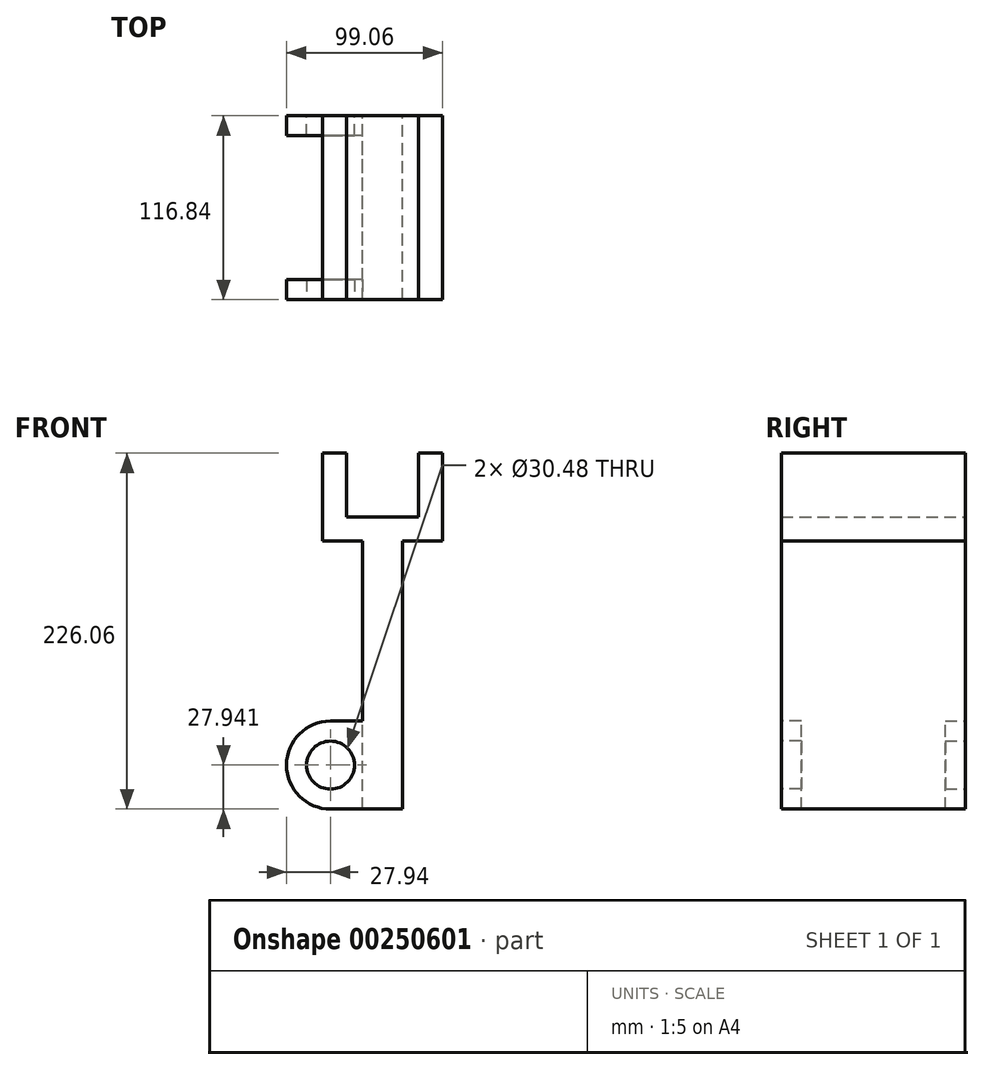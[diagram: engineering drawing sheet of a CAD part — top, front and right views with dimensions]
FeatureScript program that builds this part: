
annotation { "Feature Type Name" : "Feature", "Feature Type Description" : "" }
export const myFeature = defineFeature(function(context is Context, id is Id, definition is map)
    precondition{}
    {
        {
            var Q0;
            Q0=qCreatedBy(makeId("Front.planeOp"),FACE);
            var sketch = newSketch(context, id + "F0", { "sketchPlane" : qUnion([Q0])});
            skLineSegment(sketch, "E0", {"start": v(0, 86.1) * mm, "end": v(-38.1, 86.1) * mm});
            skLineSegment(sketch, "E1", {"start": v(-38.1, 86.1) * mm, "end": v(-38.1, 141.98) * mm});
            skLineSegment(sketch, "E2", {"start": v(-38.1, 141.98) * mm, "end": v(-22.86, 141.98) * mm});
            skLineSegment(sketch, "E3", {"start": v(-22.86, 141.98) * mm, "end": v(-22.86, 101.34) * mm});
            skLineSegment(sketch, "E4", {"start": v(-22.86, 101.34) * mm, "end": v(0, 101.34) * mm});
            skLineSegment(sketch, "E5", {"start": v(0, 163.08) * mm, "end": v(0, 27.94) * mm, "construction": true});
            skLineSegment(sketch, "E6.MirrorCS", {"start": v(0, 86.1) * mm, "end": v(38.1, 86.1) * mm});
            skLineSegment(sketch, "E7.MirrorCS", {"start": v(38.1, 86.1) * mm, "end": v(38.1, 141.98) * mm});
            skLineSegment(sketch, "E8.MirrorCS", {"start": v(38.1, 141.98) * mm, "end": v(22.86, 141.98) * mm});
            skLineSegment(sketch, "E9.MirrorCS", {"start": v(22.86, 141.98) * mm, "end": v(22.86, 101.34) * mm});
            skLineSegment(sketch, "E10.MirrorCS", {"start": v(22.86, 101.34) * mm, "end": v(0, 101.34) * mm});
            skSolve(sketch);
        }
        {
            var Q0;
            Q0=makeQuery(id+"F0.imprint","IMPRINT",FACE,{"disambiguationData":[TD([[makeQuery(id+"F0.imprint","IMPRINT",EDGE,{"derivedFrom":sQuery(id+"F0.wireOp",EDGE,"E0")}),-1.0]])]});
            extrude(context, id + "F1", {"entities" : qUnion([Q0]), "depth" : 116.84 * mm});
        }
        {
            var Q0;
            Q0=makeQuery(id+"F1.opExtrude","SWEPT_FACE",FACE,{"disambiguationData":[OSD([sQuery(id+"F0.wireOp",EDGE,"E0"),sQuery(id+"F0.wireOp",EDGE,"E6.MirrorCS")])]});
            var sketch = newSketch(context, id + "F2", { "sketchPlane" : qUnion([Q0])});
            skPoint(sketch, "E11.middle", {"position": v(0, 82.12) * mm});
            skLineSegment(sketch, "E12.bottom", {"start": v(12.7, 116.84) * mm, "end": v(-12.7, 116.84) * mm});
            skLineSegment(sketch, "E12.top", {"start": v(12.7, 0) * mm, "end": v(-12.7, 0) * mm});
            skLineSegment(sketch, "E12.left", {"start": v(12.7, 116.84) * mm, "end": v(12.7, 0) * mm});
            skLineSegment(sketch, "E12.right", {"start": v(-12.7, 116.84) * mm, "end": v(-12.7, 0) * mm});
            skPoint(sketch, "E12.middle", {"position": v(0, 58.42) * mm});
            skSolve(sketch);
        }
        {
            var Q0;
            Q0=makeQuery(id+"F2.imprint","IMPRINT",FACE,{"disambiguationData":[TD([[makeQuery(id+"F2.imprint","IMPRINT",EDGE,{"derivedFrom":sQuery(id+"F2.wireOp",EDGE,"E12.bottom")}),1.0]])]});
            extrude(context, id + "F3", {"entities" : qUnion([Q0]), "operationType" : NewBodyOperationType.ADD, "depth" : 170.18 * mm});
        }
        {
            var Q0;
            Q0=makeQuery(id+"F3.boolean.opBoolean","MERGE",FACE,{"derivedFrom":[makeQuery(id+"F1.opExtrude","CAP_FACE",FACE,{"disambiguationData":[OSD([sQuery(id+"F0.wireOp",EDGE,"E0"),sQuery(id+"F0.wireOp",EDGE,"E1"),sQuery(id+"F0.wireOp",EDGE,"E2"),sQuery(id+"F0.wireOp",EDGE,"E3"),sQuery(id+"F0.wireOp",EDGE,"E4"),sQuery(id+"F0.wireOp",EDGE,"E6.MirrorCS"),sQuery(id+"F0.wireOp",EDGE,"E7.MirrorCS"),sQuery(id+"F0.wireOp",EDGE,"E8.MirrorCS"),sQuery(id+"F0.wireOp",EDGE,"E9.MirrorCS"),sQuery(id+"F0.wireOp",EDGE,"E10.MirrorCS")])],"isStart":true}),makeQuery(id+"F3.opExtrude","SWEPT_FACE",FACE,{"disambiguationData":[OSD([sQuery(id+"F2.wireOp",EDGE,"E12.top")])]})]});
            var sketch = newSketch(context, id + "F4", { "sketchPlane" : qUnion([Q0])});
            skArc(sketch, "E13", {"start": v(33.02, -84.08) * mm, "mid": v(60.96, -56.14) * mm, "end": v(33.02, -28.2) * mm});
            skLineSegment(sketch, "E14", {"start": v(-12.7, -84.08) * mm, "end": v(34.27, -84.08) * mm});
            skLineSegment(sketch, "E15", {"start": v(33.02, -28.2) * mm, "end": v(-12.77, -28.2) * mm});
            skCircle(sketch, "E16", {"center": v(33.02, -56.14) * mm, "radius": 15.24 * mm});
            skLineSegment(sketch, "E17", {"start": v(-12.77, -28.2) * mm, "end": v(-12.7, -84.08) * mm});
            skSolve(sketch);
        }
        {
            var Q0;
            {var subQ1=sQuery(id+"F4.wireOp",EDGE,"E13");Q0=makeQuery(id+"F4.imprint","IMPRINT",FACE,{"disambiguationData":[TD([[makeQuery(id+"F4.imprint","IMPRINT",EDGE,{"derivedFrom":subQ1}),1.0]])]});}
            extrude(context, id + "F5", {"entities" : qUnion([Q0]), "oppositeDirection" : true, "depth" : 12.7 * mm});
        }
        {
            var Q0;
            Q0=qCreatedBy(makeId("Front.planeOp"),FACE);
            cPlane(context, id + "F6", {"entities" : qUnion([Q0]), "cplaneType" : CPlaneType.OFFSET, "offset" : 58.42 * mm, "width" : 152.4 * mm, "height" : 152.4 * mm});
        }
        {
            var Q0;
            Q0=makeQuery(id+"F5.opExtrude","SWEPT_BODY",BODY,{"disambiguationData":[OSD([sQuery(id+"F0.wireOp",EDGE,"E0"),sQuery(id+"F0.wireOp",EDGE,"E6.MirrorCS"),sQuery(id+"F2.wireOp",EDGE,"E12.top"),sQuery(id+"F2.wireOp",EDGE,"E12.right"),sQuery(id+"F4.wireOp",EDGE,"E13"),sQuery(id+"F4.wireOp",EDGE,"E14"),sQuery(id+"F4.wireOp",EDGE,"E15"),sQuery(id+"F4.wireOp",EDGE,"E16")])]});
            var Q1;
            Q1=qCreatedBy(id+"F6.planeOp",FACE);
            mirror(context, id + "F7", {"operationType" : NewBodyOperationType.ADD, "entities" : qUnion([Q0]), "mirrorPlane" : qUnion([Q1])});
        }
    });
